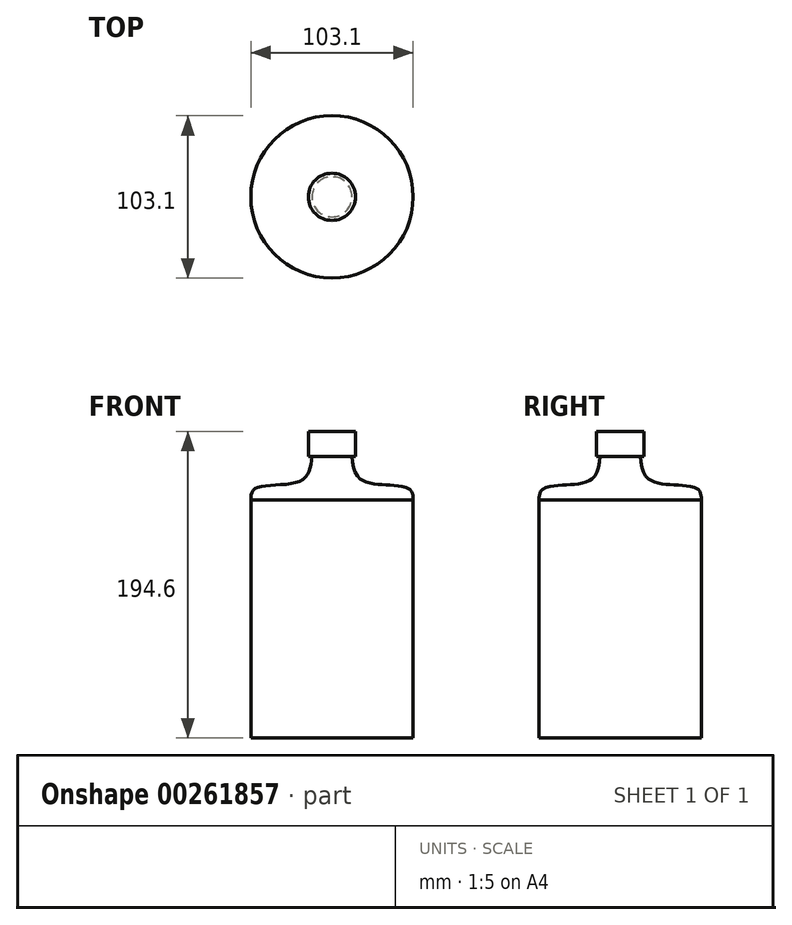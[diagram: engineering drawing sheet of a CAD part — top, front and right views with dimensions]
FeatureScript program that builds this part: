
annotation { "Feature Type Name" : "Feature", "Feature Type Description" : "" }
export const myFeature = defineFeature(function(context is Context, id is Id, definition is map)
    precondition{}
    {
        {
            var Q0;
            Q0=qCreatedBy(makeId("Front.planeOp"),FACE);
            var sketch = newSketch(context, id + "F0", { "sketchPlane" : qUnion([Q0])});
            skLineSegment(sketch, "E0", {"start": v(0, 105.07) * mm, "end": v(0, -115.8) * mm, "construction": true});
            skLineSegment(sketch, "E1", {"start": v(0, -115.8) * mm, "end": v(-51.55, -115.8) * mm});
            skLineSegment(sketch, "E2", {"start": v(-51.55, -115.8) * mm, "end": v(-51.55, 35.35) * mm});
            skFitSpline(sketch, "E3", {"points": [v(-51.55, 35.35) * mm, v(-48.42, 42.8) * mm, v(-19.8, 47.5) * mm, v(-12.75, 62.79) * mm], "startDerivative": vector(1.32, 38.3) * mm, "endDerivative": vector(6.59, 56) * mm});
            skLineSegment(sketch, "E4", {"start": v(-12.75, 62.79) * mm, "end": v(-14.98, 62.79) * mm});
            skLineSegment(sketch, "E5", {"start": v(-14.98, 62.79) * mm, "end": v(-14.98, 78.8) * mm});
            skLineSegment(sketch, "E6", {"start": v(-14.98, 78.8) * mm, "end": v(0, 78.8) * mm});
            skSolve(sketch);
        }
        {
            var Q0;
            Q0=sQuery(id+"F0.wireOp",EDGE,"E3");
            var Q1;
            Q1=sQuery(id+"F0.wireOp",EDGE,"E2");
            var Q2;
            Q2=sQuery(id+"F0.wireOp",EDGE,"E6");
            var Q3;
            Q3=sQuery(id+"F0.wireOp",EDGE,"E5");
            var Q4;
            Q4=sQuery(id+"F0.wireOp",EDGE,"E1");
            var Q5;
            Q5=sQuery(id+"F0.wireOp",EDGE,"E4");
            var Q6;
            Q6=sQuery(id+"F0.wireOp",EDGE,"E0");
            revolve(context, id + "F1", {"bodyType" : ToolBodyType.SURFACE, "surfaceEntities" : qUnion([Q0, Q1, Q2, Q3, Q4, Q5]), "axis" : qUnion([Q6]), "revolveType" : RevolveType.FULL});
        }
    });
